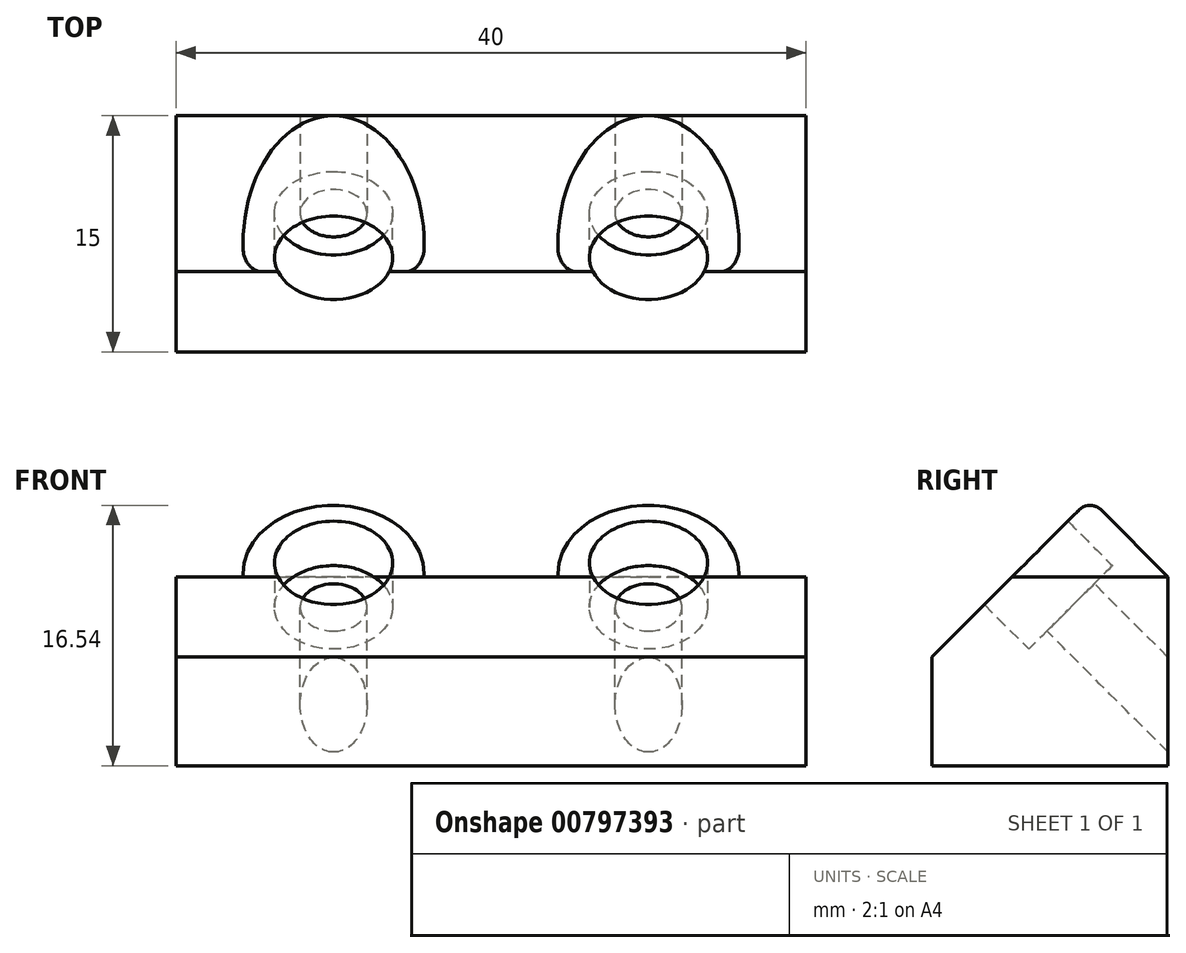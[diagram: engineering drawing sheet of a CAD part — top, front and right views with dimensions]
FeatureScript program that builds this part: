
annotation { "Feature Type Name" : "Feature", "Feature Type Description" : "" }
export const myFeature = defineFeature(function(context is Context, id is Id, definition is map)
    precondition{}
    {
        {
            var Q0;
            Q0=qCreatedBy(makeId("Top.planeOp"),FACE);
            var sketch = newSketch(context, id + "F0", { "sketchPlane" : qUnion([Q0])});
            skLineSegment(sketch, "E0", {"start": v(-19.63, 0) * mm, "end": v(19.5, 0) * mm});
            skSolve(sketch);
        }
        {
            var Q0;
            Q0=sQuery(id+"F0.wireOp",EDGE,"E0");
            cPlane(context, id + "F1", {"entities" : qUnion([Q0]), "cplaneType" : CPlaneType.LINE_ANGLE, "offset" : 25 * mm, "angle" : 45 * degree, "oppositeDirection" : true, "width" : 150 * mm, "height" : 150 * mm});
        }
        {
            var Q0;
            Q0=qCreatedBy(id+"F1.planeOp",FACE);
            var sketch = newSketch(context, id + "F2", { "sketchPlane" : qUnion([Q0])});
            skCircle(sketch, "E1", {"center": v(0, 0) * mm, "radius": 3.75 * mm});
            skCircle(sketch, "E2.0", {"center": v(0, 0) * mm, "radius": 5.75 * mm});
            skSolve(sketch);
        }
        {
            var Q0;
            Q0=makeQuery(id+"F2.imprint","IMPRINT",FACE,{"disambiguationData":[TD([[makeQuery(id+"F2.imprint","IMPRINT",EDGE,{"derivedFrom":sQuery(id+"F2.wireOp",EDGE,"E1")}),-1.0]])]});
            var Q1;
            Q1=makeQuery(id+"F2.imprint","IMPRINT",FACE,{"disambiguationData":[TD([[makeQuery(id+"F2.imprint","IMPRINT",EDGE,{"derivedFrom":sQuery(id+"F2.wireOp",EDGE,"E1")}),1.0]])]});
            extrude(context, id + "F3", {"entities" : qUnion([Q0, Q1]), "depth" : 3 * mm, "offsetDistance" : 25 * mm});
        }
        {
            var Q0;
            Q0=makeQuery(id+"F2.imprint","IMPRINT",FACE,{"disambiguationData":[TD([[makeQuery(id+"F2.imprint","IMPRINT",EDGE,{"derivedFrom":sQuery(id+"F2.wireOp",EDGE,"E1")}),-1.0]])]});
            extrude(context, id + "F4", {"entities" : qUnion([Q0]), "operationType" : NewBodyOperationType.ADD, "oppositeDirection" : true, "depth" : 4 * mm, "offsetDistance" : 25 * mm});
        }
        {
            var Q0;
            Q0=qCreatedBy(makeId("Top.planeOp"),FACE);
            var sketch = newSketch(context, id + "F5", { "sketchPlane" : qUnion([Q0])});
            skLineSegment(sketch, "E3", {"start": v(0, 11.18) * mm, "end": v(0, -14.08) * mm});
            skSolve(sketch);
        }
        {
            var Q0;
            Q0=sQuery(id+"F5.wireOp",EDGE,"E3");
            cPlane(context, id + "F6", {"entities" : qUnion([Q0]), "cplaneType" : CPlaneType.LINE_ANGLE, "offset" : 25 * mm, "angle" : 90 * degree, "width" : 150 * mm, "height" : 150 * mm});
        }
        {
            var Q0;
            Q0=qCreatedBy(id+"F6.planeOp",FACE);
            var sketch = newSketch(context, id + "F7", { "sketchPlane" : qUnion([Q0])});
            skLineSegment(sketch, "E4.0", {"start": v(6.19, 1.94) * mm, "end": v(-1.94, -6.19) * mm});
            skLineSegment(sketch, "E5.bottom", {"start": v(6.19, 1.94) * mm, "end": v(-8.81, 1.94) * mm});
            skLineSegment(sketch, "E5.top", {"start": v(6.19, -10.06) * mm, "end": v(-8.81, -10.06) * mm});
            skLineSegment(sketch, "E5.left", {"start": v(6.19, 1.94) * mm, "end": v(6.19, -10.06) * mm});
            skLineSegment(sketch, "E5.right", {"start": v(-8.81, 1.94) * mm, "end": v(-8.81, -10.06) * mm});
            skSolve(sketch);
        }
        {
            var Q0;
            Q0=makeQuery(id+"F7.imprint","IMPRINT",FACE,{"disambiguationData":[TD([[makeQuery(id+"F7.imprint","IMPRINT",EDGE,{"derivedFrom":sQuery(id+"F7.wireOp",EDGE,"E5.bottom")}),1.0]])]});
            extrude(context, id + "F8", {"entities" : qUnion([Q0]), "operationType" : NewBodyOperationType.ADD, "depth" : 10 * mm, "offsetDistance" : 25 * mm, "hasSecondDirection" : true, "secondDirectionOppositeDirection" : true, "secondDirectionDepth" : 10 * mm});
        }
        {
            var Q0;
            Q0=qCreatedBy(id+"F1.planeOp",FACE);
            var sketch = newSketch(context, id + "F9", { "sketchPlane" : qUnion([Q0])});
            skCircle(sketch, "E6.0", {"center": v(0, 0) * mm, "radius": 3.75 * mm});
            skSolve(sketch);
        }
        {
            var Q0;
            Q0 = qSketchRegion(id + "F9", true);
            extrude(context, id + "F10", {"entities" : qUnion([Q0]), "operationType" : NewBodyOperationType.REMOVE, "oppositeDirection" : true, "depth" : 25 * mm, "offsetDistance" : 25 * mm});
        }
        {
            var Q0;
            Q0=qCreatedBy(id+"F1.planeOp",FACE);
            var sketch = newSketch(context, id + "F11", { "sketchPlane" : qUnion([Q0])});
            skPoint(sketch, "E7.0", {"position": v(0, 0) * mm});
            skSolve(sketch);
        }
        {
            var Q0;
            Q0=sQuery(id+"F11.wireOp",VERTEX,"E7.0");
            var Q1;
            Q1=makeQuery(id+"F3.opExtrude","SWEPT_BODY",BODY,{"disambiguationData":[OSD([sQuery(id+"F2.wireOp",EDGE,"E2.0")])]});
            hole(context, id + "F12", {"style" : HoleStyle.SIMPLE, "endStyle" : HoleEndStyle.THROUGH, "oppositeDirection" : true, "holeDiameter" : 4.25 * mm, "majorDiameter" : 5 * mm, "isTappedThrough" : true, "tappedDepth" : 12 * mm, "tapClearance" : 3, "locations" : qUnion([Q0]), "scope" : qUnion([Q1])});
        }
        {
            var Q0;
            Q0=makeQuery(id+"F3.opExtrude","SWEPT_BODY",BODY,{"disambiguationData":[OSD([sQuery(id+"F2.wireOp",EDGE,"E2.0")])]});
            transform(context, id + "F13", {"entities" : qUnion([Q0]), "transformType" : TransformType.TRANSLATION_3D, "dx" : -20 * mm, "dy" : 0 * mm, "dz" : 0 * mm, "makeCopy" : true});
        }
        {
            var Q0;
            Q0=makeQuery(id+"F3.opExtrude","SWEPT_BODY",BODY,{"disambiguationData":[OSD([sQuery(id+"F2.wireOp",EDGE,"E2.0")])]});
            var Q1;
            Q1=makeQuery(id+"F13.opPattern","COPY",BODY,{"derivedFrom":makeQuery(id+"F3.opExtrude","SWEPT_BODY",BODY,{"disambiguationData":[OSD([sQuery(id+"F2.wireOp",EDGE,"E2.0")])]}),"instanceName":"1"});
            booleanBodies(context, id + "F14", {"operationType" : BooleanOperationType.UNION, "tools" : qUnion([Q0, Q1])});
        }
        {
            var Q0;
            {var subQ0=makeQuery(id+"F8.opExtrude","SWEPT_EDGE",EDGE,{"disambiguationData":[OSD([sQuery(id+"F7.wireOp",EDGE,"E5.bottom"),sQuery(id+"F7.wireOp",EDGE,"E5.right")])]});Q0=makeQuery(id+"F14.opBoolean","MERGE",EDGE,{"derivedFrom":[subQ0,makeQuery(id+"F13.opPattern","COPY",EDGE,{"derivedFrom":subQ0,"instanceName":"1"})]});}
            chamfer(context, id + "F15", {"entities" : qUnion([Q0]), "width" : 5.1 * mm, "tangentPropagation" : true});
        }
        {
            var Q0;
            Q0=makeQuery(id+"F13.opPattern","COPY",EDGE,{"derivedFrom":makeQuery(id+"F4.opExtrude","CAP_EDGE",EDGE,{"disambiguationData":[OSD([sQuery(id+"F2.wireOp",EDGE,"E2.0")])],"isStart":false}),"instanceName":"1"});
            var Q1;
            Q1=makeQuery(id+"F4.opExtrude","CAP_EDGE",EDGE,{"disambiguationData":[OSD([sQuery(id+"F2.wireOp",EDGE,"E2.0")])],"isStart":false});
            fillet(context, id + "F16", {"entities" : qUnion([Q0, Q1]), "radius" : 1 * mm, "tangentPropagation" : true, "allowEdgeOverflow" : false});
        }
    });
